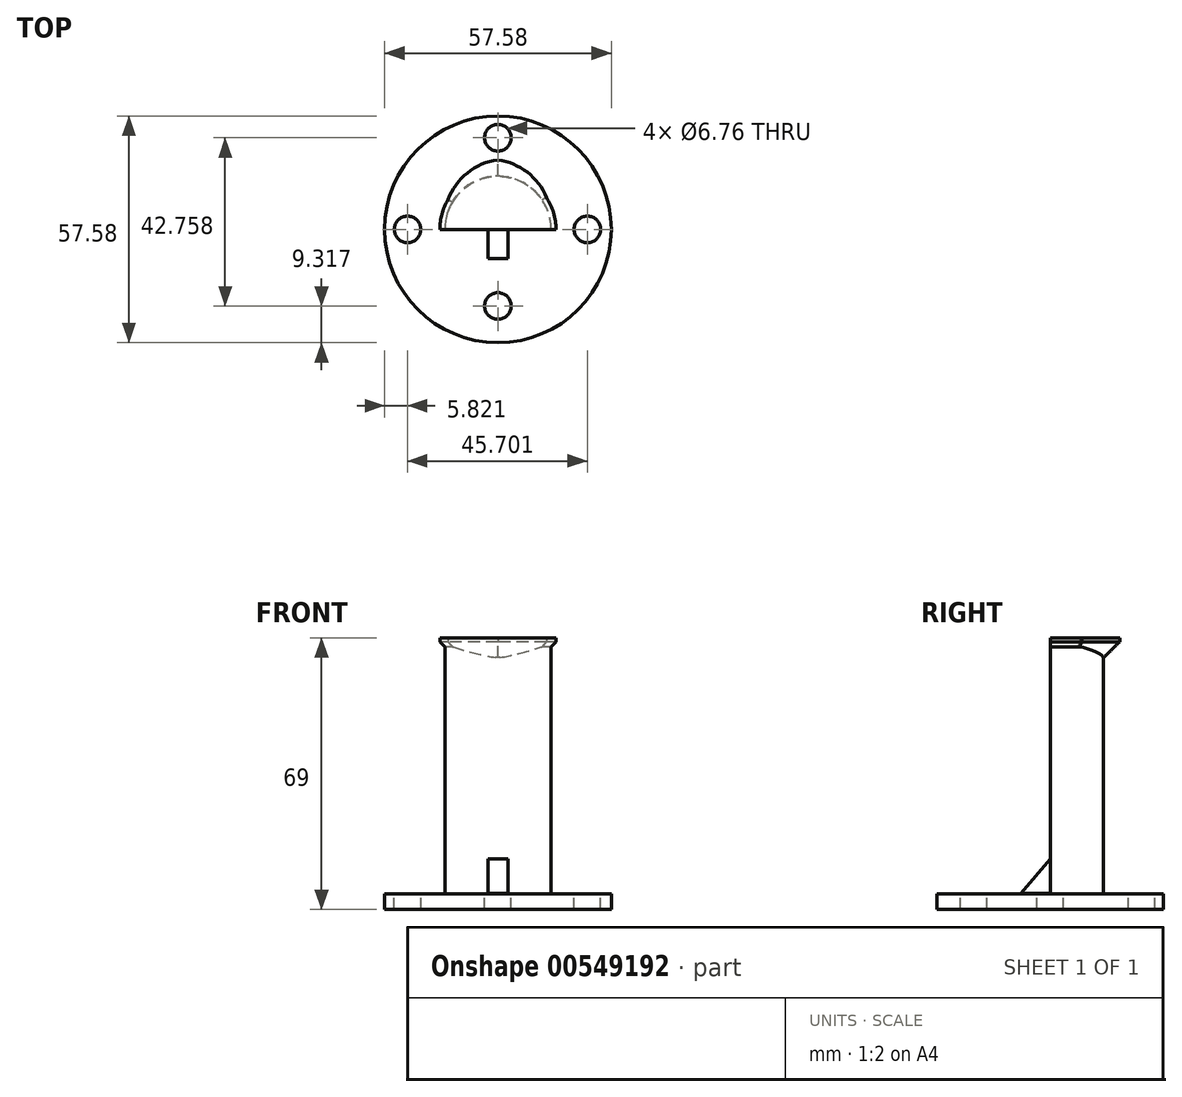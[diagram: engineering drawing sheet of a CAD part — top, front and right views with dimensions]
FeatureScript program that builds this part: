
annotation { "Feature Type Name" : "Feature", "Feature Type Description" : "" }
export const myFeature = defineFeature(function(context is Context, id is Id, definition is map)
    precondition{}
    {
        {
            var Q0;
            Q0=qCreatedBy(makeId("Top.planeOp"),FACE);
            var sketch = newSketch(context, id + "F0", { "sketchPlane" : qUnion([Q0])});
            skCircle(sketch, "E0", {"center": v(0, 0) * mm, "radius": 28.8 * mm});
            skSolve(sketch);
        }
        {
            var Q0;
            Q0=makeQuery(id+"F0.imprint","IMPRINT",FACE,{"disambiguationData":[TD([[makeQuery(id+"F0.imprint","IMPRINT",EDGE,{"derivedFrom":sQuery(id+"F0.wireOp",EDGE,"E0")}),1.0]])]});
            extrude(context, id + "F1", {"entities" : qUnion([Q0]), "depth" : 4 * mm, "offsetDistance" : 25 * mm});
        }
        {
            var Q0;
            Q0=makeQuery(id+"F1.opExtrude","CAP_FACE",FACE,{"disambiguationData":[OSD([sQuery(id+"F0.wireOp",EDGE,"E0")])],"isStart":false});
            var sketch = newSketch(context, id + "F2", { "sketchPlane" : qUnion([Q0])});
            skArc(sketch, "E1", {"start": v(13.5, 0) * mm, "mid": v(0, 13.5) * mm, "end": v(-13.5, 0) * mm});
            skLineSegment(sketch, "E2", {"start": v(-13.5, 0) * mm, "end": v(13.5, 0) * mm});
            skSolve(sketch);
        }
        {
            var Q0;
            Q0=makeQuery(id+"F2.imprint","IMPRINT",FACE,{"disambiguationData":[TD([[makeQuery(id+"F2.imprint","IMPRINT",EDGE,{"derivedFrom":sQuery(id+"F2.wireOp",EDGE,"E1")}),1.0]])]});
            extrude(context, id + "F3", {"entities" : qUnion([Q0]), "operationType" : NewBodyOperationType.ADD, "depth" : 60 * mm, "offsetDistance" : 25 * mm});
        }
        {
            var Q0;
            Q0=qCreatedBy(makeId("Right.planeOp"),FACE);
            var sketch = newSketch(context, id + "F4", { "sketchPlane" : qUnion([Q0])});
            skLineSegment(sketch, "E3", {"start": v(0, 12.82) * mm, "end": v(-7.4, 4.08) * mm});
            skLineSegment(sketch, "E4", {"start": v(-7.4, 4.08) * mm, "end": v(0, 4.08) * mm});
            skLineSegment(sketch, "E5", {"start": v(0, 4.08) * mm, "end": v(0, 12.82) * mm});
            skSolve(sketch);
        }
        {
            var Q0;
            Q0=makeQuery(id+"F4.imprint","IMPRINT",FACE,{"disambiguationData":[TD([[makeQuery(id+"F4.imprint","IMPRINT",EDGE,{"derivedFrom":sQuery(id+"F4.wireOp",EDGE,"E3")}),1.0]])]});
            extrude(context, id + "F5", {"entities" : qUnion([Q0]), "operationType" : NewBodyOperationType.ADD, "endBound" : BoundingType.SYMMETRIC, "depth" : 5 * mm, "offsetDistance" : 25 * mm});
        }
        {
            var Q0;
            Q0=makeQuery(id+"F3.opExtrude","CAP_FACE",FACE,{"disambiguationData":[OSD([sQuery(id+"F2.wireOp",EDGE,"E1"),sQuery(id+"F2.wireOp",EDGE,"E2")])],"isStart":false});
            var sketch = newSketch(context, id + "F6", { "sketchPlane" : qUnion([Q0])});
            skArc(sketch, "E6", {"start": v(14.75, 0) * mm, "mid": v(14.14, 4.21) * mm, "end": v(12.34, 8.08) * mm});
            skLineSegment(sketch, "E7", {"start": v(-14.75, 0) * mm, "end": v(14.75, 0) * mm});
            skArc(sketch, "E8", {"start": v(0, 17.65) * mm, "mid": v(-7.76, 14.36) * mm, "end": v(-12.7, 7.52) * mm});
            skArc(sketch, "E9", {"start": v(12.34, 8.08) * mm, "mid": v(7.45, 14.52) * mm, "end": v(0, 17.65) * mm});
            skArc(sketch, "E10.trimOffspring", {"start": v(-12.7, 7.52) * mm, "mid": v(-14.23, 3.9) * mm, "end": v(-14.75, 0) * mm});
            skSolve(sketch);
        }
        {
            var Q0;
            {var subQ0=sQuery(id+"F6.wireOp",EDGE,"E6");Q0=makeQuery(id+"F6.imprint","IMPRINT",FACE,{"disambiguationData":[TD([[makeQuery(id+"F6.imprint","IMPRINT",EDGE,{"derivedFrom":subQ0}),1.0]])]});}
            var Q1;
            {var subQ1=makeQuery(id+"F3.opExtrude","CAP_EDGE",EDGE,{"disambiguationData":[OSD([sQuery(id+"F2.wireOp",EDGE,"E1")])],"isStart":false});Q1=makeQuery(id+"F6.imprint","IMPRINT",FACE,{"disambiguationData":[TD([[makeQuery(id+"F6.imprint","IMPRINT",EDGE,{"derivedFrom":subQ1}),1.0]])]});}
            extrude(context, id + "F7", {"entities" : qUnion([Q0, Q1]), "operationType" : NewBodyOperationType.ADD, "depth" : 5 * mm, "offsetDistance" : 25 * mm});
        }
        {
            var Q0;
            Q0=makeQuery(id+"F1.opExtrude","CAP_FACE",FACE,{"disambiguationData":[OSD([sQuery(id+"F0.wireOp",EDGE,"E0")])],"isStart":false});
            var sketch = newSketch(context, id + "F8", { "sketchPlane" : qUnion([Q0])});
            skLineSegment(sketch, "E11", {"start": v(0, -19.47) * mm, "end": v(0, 23.29) * mm});
            skPoint(sketch, "E11.endSnap0", {"position": v(0, 13.5) * mm});
            skLineSegment(sketch, "E12", {"start": v(0, 23.29) * mm, "end": v(-22.97, 0) * mm});
            skLineSegment(sketch, "E13", {"start": v(-22.97, 0) * mm, "end": v(22.73, 0) * mm});
            skSolve(sketch);
        }
        {
            var Q0;
            Q0=sQuery(id+"F8.wireOp",VERTEX,"E11.start");
            var Q1;
            Q1=sQuery(id+"F8.wireOp",VERTEX,"E13.start");
            var Q2;
            Q2=sQuery(id+"F8.wireOp",VERTEX,"E12.start");
            var Q3;
            Q3=sQuery(id+"F8.wireOp",VERTEX,"E13.end");
            var Q4;
            Q4=makeQuery(id+"F1.opExtrude","SWEPT_BODY",BODY,{"disambiguationData":[OSD([sQuery(id+"F0.wireOp",EDGE,"E0")])]});
            hole(context, id + "F9", {"style" : HoleStyle.SIMPLE, "endStyle" : HoleEndStyle.THROUGH, "standardTappedOrClearance" : lookupTablePath({ "standard" : "ANSI", "fit" : "Normal (ASME)", "size" : "1/4", "type" : "Clearance" }), "standardBlindInLast" : lookupTablePath({ "fit" : "Free", "standard" : "ANSI", "size" : "1/4", "type" : "Clearance" }), "holeDiameter" : 6.76 * mm, "isTappedThrough" : true, "tappedDepth" : 12 * mm, "tapClearance" : 3, "locations" : qUnion([Q0, Q1, Q2, Q3]), "scope" : qUnion([Q4])});
        }
        {
            var Q0;
            Q0=makeQuery(id+"F7.opExtrude","CAP_EDGE",EDGE,{"disambiguationData":[OSD([sQuery(id+"F6.wireOp",EDGE,"E10.trimOffspring")])],"isStart":true});
            var Q1;
            Q1=makeQuery(id+"F7.opExtrude","CAP_EDGE",EDGE,{"disambiguationData":[OSD([sQuery(id+"F6.wireOp",EDGE,"E8")])],"isStart":true});
            var Q2;
            Q2=makeQuery(id+"F7.opExtrude","CAP_EDGE",EDGE,{"disambiguationData":[OSD([sQuery(id+"F6.wireOp",EDGE,"E9")])],"isStart":true});
            var Q3;
            Q3=makeQuery(id+"F7.opExtrude","CAP_EDGE",EDGE,{"disambiguationData":[OSD([sQuery(id+"F6.wireOp",EDGE,"E6")])],"isStart":true});
            chamfer(context, id + "F10", {"entities" : qUnion([Q0, Q1, Q2, Q3]), "width" : 4 * mm, "tangentPropagation" : true});
        }
    });
